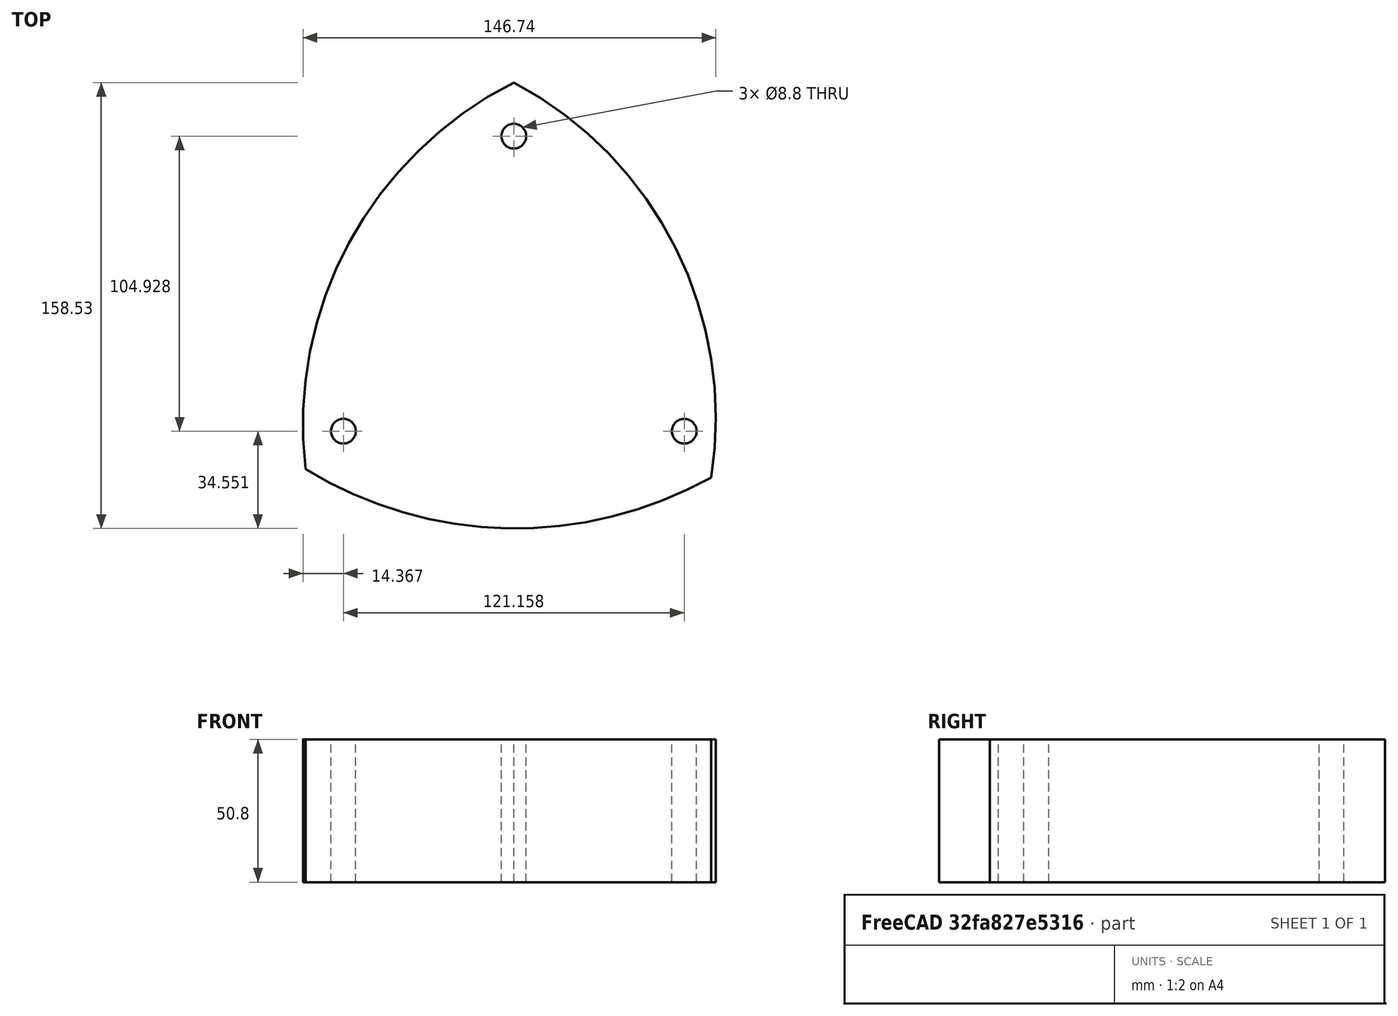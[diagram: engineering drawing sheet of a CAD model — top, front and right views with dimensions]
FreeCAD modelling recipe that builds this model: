
FCSTD DOCUMENT  (FreeCAD 0.18R4 (GitTag))
Label: Front Spacers
License: All rights reserved
LicenseURL: http://en.wikipedia.org/wiki/All_rights_reserved
objects: Sketcher::SketchObject×3, PartDesign::Pad×1, PartDesign::Hole×1, PartDesign::Body×1
note: 8 computed .brp shape members not serialized (recipe doc carries the construction recipe); baked Part::Feature solids carry a one-line shape summary decoded from their .brp

FEATURE [Sketcher::SketchObject] Sketch  label="Holes"
  MapMode = 2
  Placement = pos=(0,0,0) rot=(0,1,0;3.14159rad)
  Support = -> [Sketch]
  sketch-geometry (3):
    g0: Circle CenterX=-60.575 CenterY=-34.9791 CenterZ=0 NormalX=0 NormalY=0 NormalZ=1 AngleXU=0 Radius=4.318
    g1: Circle CenterX=0 CenterY=69.9491 CenterZ=0 NormalX=0 NormalY=0 NormalZ=1 AngleXU=0 Radius=4.318
    g2: Circle CenterX=60.583 CenterY=-34.9653 CenterZ=0 NormalX=0 NormalY=0 NormalZ=1 AngleXU=0 Radius=4.318
  constraints (6):
    c: Radius(g0) = 4.318  'M8 Thru-Hole'
    c: Equal(g0,g1) = 9  'M8 Thru-Hole2'
    c: Equal(g1,g2)  'M8 Thru-Hole1'
    c: Distance(g1,g0) = 121.158  'Bolt Pattern3'
    c: Distance(g2,g0) = 121.158  'Bolt Pattern1'
    c: PointOnObject(g1,g-2)
FEATURE [Sketcher::SketchObject] Sketch001
  ExternalGeometry = -> [Sketch]
  MapMode = 5
  Support = -> [XY_Plane001]
  sketch-geometry (3):
    g0: ArcOfCircle CenterX=61.4032 CenterY=-32.7486 CenterZ=0 NormalX=0 NormalY=0 NormalZ=1 AngleXU=0 Radius=136.356 StartAngle=2.03792 EndAngle=3.257
    g1: ArcOfCircle CenterX=-63.1229 CenterY=-30.2344 CenterZ=0 NormalX=0 NormalY=0 NormalZ=1 AngleXU=0 Radius=134.912 StartAngle=6.12518 EndAngle=7.36709
    g2: ArcOfCircle CenterX=0.606228 CenterY=73.2133 CenterZ=0 NormalX=0 NormalY=0 NormalZ=1 AngleXU=0 Radius=142.74 StartAngle=4.16203 EndAngle=5.22094
FEATURE [PartDesign::Pad] Pad
  Length = 50.8
  Length2 = 100.076
  Profile = -> Sketch001
  Type = 0
FEATURE [PartDesign::Hole] Hole
  BaseFeature = -> Pad
  Depth = 80
  DepthType = 1
  Diameter = 8.8
  DrillPoint = 1
  DrillPointAngle = 118
  HoleCutCountersinkAngle = 90
  HoleCutDepth = 0
  HoleCutDiameter = 8
  HoleCutType = 0
  ModelActualThread = false
  Profile = -> Sketch
  Tapered = false
  TaperedAngle = 90
  ThreadAngle = 0
  ThreadClass = 0
  ThreadCutOffInner = 0
  ThreadCutOffOuter = 0
  ThreadDirection = 0
  ThreadFit = 0
  ThreadPitch = 0
  ThreadSize = 8
  ThreadType = 1
  Threaded = false
FEATURE [Sketcher::SketchObject] Sketch002
  MapMode = 5
  Support = -> [XY_Plane001]
  sketch-geometry (1):
    g0: Circle CenterX=-0.001488 CenterY=-0.000858 CenterZ=0 NormalX=0 NormalY=0 NormalZ=1 AngleXU=0 Radius=53.34
  constraints (1):
    c: Radius(g0) = 53.34
FEATURE [PartDesign::Body] Body001
  Group = -> [Sketch,Sketch001,Pad,Hole,Sketch002]
  Origin = -> Origin001
  Tip = -> Hole
